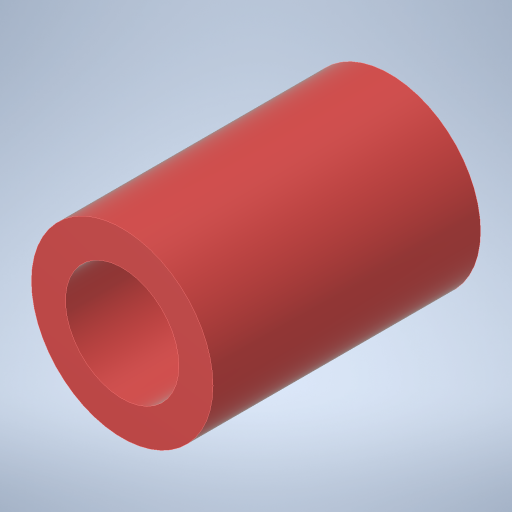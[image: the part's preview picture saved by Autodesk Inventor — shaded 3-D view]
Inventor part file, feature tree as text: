
AUTODESK INVENTOR PART (.ipt)
format: ipt  version: 2023.3 (Build 273359000, 359)  size: 231,424 bytes
history: native  units: in
note: dims shown in document units (in); Inventor stores cm internally (conversion verified against a paired STEP export)
features: extrude x1, sketch x1
ambient origin geometry x8: Origin, YZ Plane, XZ Plane, XY Plane, X Axis, Y Axis, Z Axis, Center Point
bodies: Solid1 (feature_tree)
feature tree (2):
  extrude  "Extrusion1"  [1 undecoded]
  sketch  "Sketch1"  dims[d3=0.0in]
note: 1 required parameter value undecoded (feature->parameter linkage not recoverable at this tier; creation-order binding heuristic only, values carry confidence <= 0.55)
